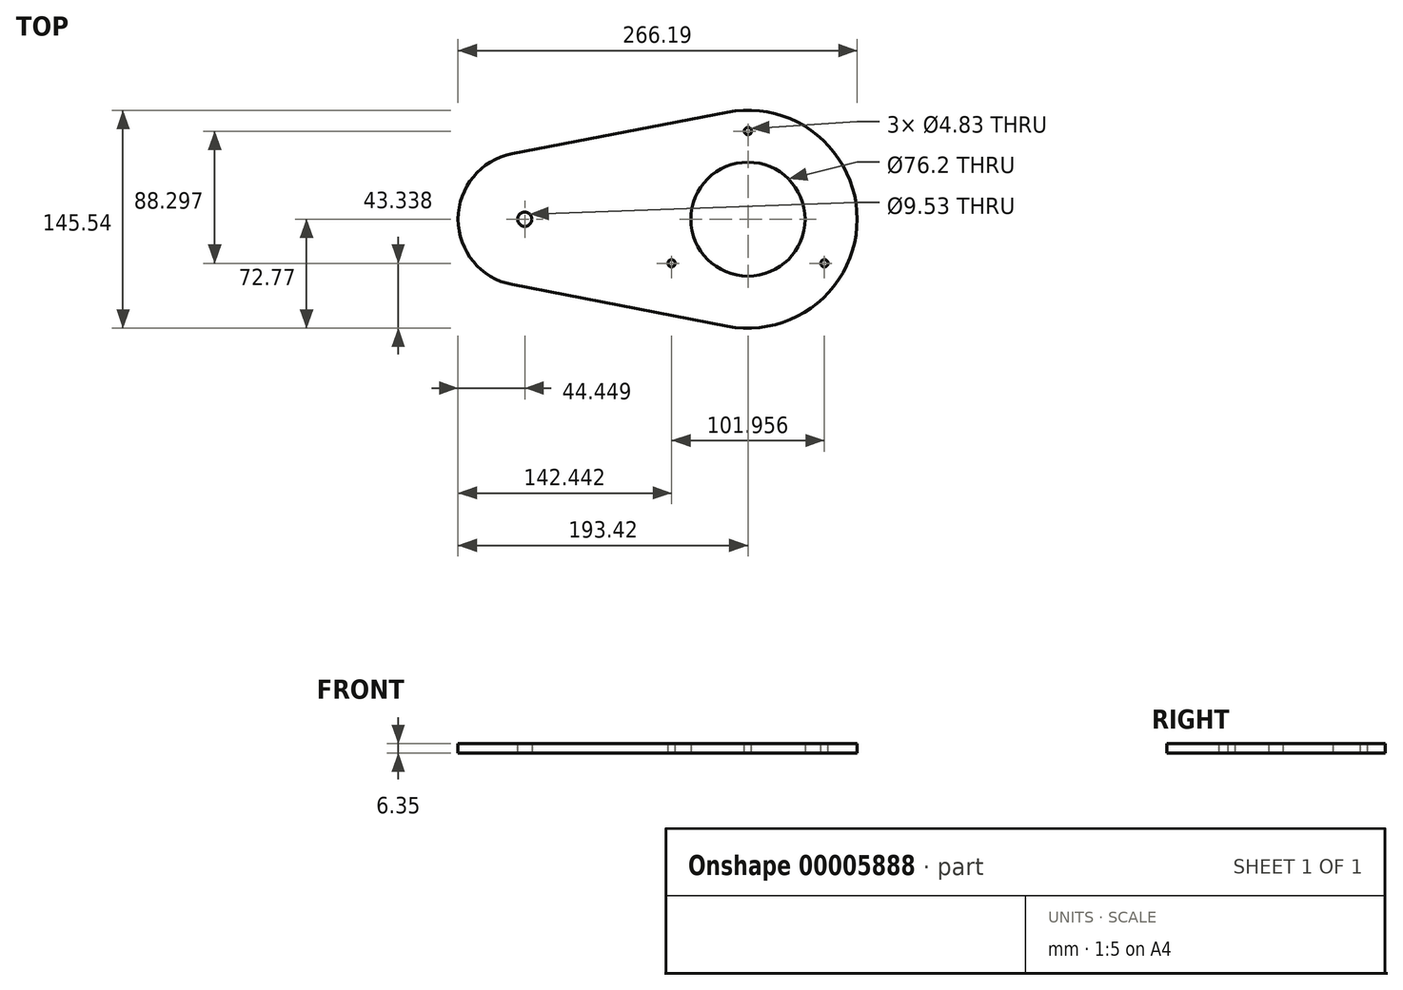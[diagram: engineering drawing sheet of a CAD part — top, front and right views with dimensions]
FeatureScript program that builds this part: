
annotation { "Feature Type Name" : "Feature", "Feature Type Description" : "" }
export const myFeature = defineFeature(function(context is Context, id is Id, definition is map)
    precondition{}
    {
        {
            var Q0;
            Q0=qCreatedBy(makeId("Top.planeOp"),FACE);
            var sketch = newSketch(context, id + "F0", { "sketchPlane" : qUnion([Q0])});
            skArc(sketch, "E0", {"start": v(-13.83, -71.44) * mm, "mid": v(72.77, 0) * mm, "end": v(-13.83, 71.44) * mm});
            skCircle(sketch, "E1", {"center": v(0, 0) * mm, "radius": 38.1 * mm});
            skLineSegment(sketch, "E2", {"start": v(0, 0) * mm, "end": v(-72.77, 0) * mm, "construction": true});
            skLineSegment(sketch, "E3", {"start": v(-72.77, 0) * mm, "end": v(-148.97, 0) * mm, "construction": true});
            skArc(sketch, "E4", {"start": v(-157.42, 43.64) * mm, "mid": v(-193.42, 0) * mm, "end": v(-157.42, -43.64) * mm});
            skLineSegment(sketch, "E5", {"start": v(-157.42, 43.64) * mm, "end": v(-13.83, 71.44) * mm});
            skLineSegment(sketch, "E6", {"start": v(-157.42, -43.64) * mm, "end": v(-13.83, -71.44) * mm});
            skCircle(sketch, "E7", {"center": v(-148.97, 0) * mm, "radius": 4.76 * mm});
            skSolve(sketch);
        }
        {
            var Q0;
            Q0=makeQuery(id+"F0.imprint","IMPRINT",FACE,{"disambiguationData":[TD([[makeQuery(id+"F0.imprint","IMPRINT",EDGE,{"derivedFrom":sQuery(id+"F0.wireOp",EDGE,"E0")}),1.0]])]});
            extrude(context, id + "F1", {"entities" : qUnion([Q0]), "depth" : 6.35 * mm});
        }
        {
            var Q0;
            Q0=makeQuery(id+"F1.opExtrude","CAP_FACE",FACE,{"disambiguationData":[OSD([sQuery(id+"F0.wireOp",EDGE,"E0"),sQuery(id+"F0.wireOp",EDGE,"E1"),sQuery(id+"F0.wireOp",EDGE,"7409aa68-249a-4d23-94e3-a1b410b62b42")])],"isStart":false});
            var sketch = newSketch(context, id + "F2", { "sketchPlane" : qUnion([Q0])});
            skLineSegment(sketch, "E8", {"start": v(0, 0) * mm, "end": v(0, 72.77) * mm, "construction": true});
            skCircle(sketch, "E9", {"center": v(0, 58.86) * mm, "radius": 4.76 * mm});
            skCircle(sketch, "E10.1.0", {"center": v(-50.98, -29.43) * mm, "radius": 4.76 * mm});
            skCircle(sketch, "E10.2.0", {"center": v(50.98, -29.43) * mm, "radius": 4.76 * mm});
            skPoint(sketch, "E10.center", {"position": v(0, 0) * mm});
            skCircle(sketch, "E11", {"center": v(0, 58.86) * mm, "radius": 2.41 * mm});
            skCircle(sketch, "E12.1.0", {"center": v(-50.98, -29.43) * mm, "radius": 2.41 * mm});
            skCircle(sketch, "E12.2.0", {"center": v(50.98, -29.43) * mm, "radius": 2.41 * mm});
            skSolve(sketch);
        }
        {
            var Q0;
            Q0=makeQuery(id+"F2.imprint","IMPRINT",FACE,{"disambiguationData":[TD([[makeQuery(id+"F2.imprint","IMPRINT",EDGE,{"derivedFrom":sQuery(id+"F2.wireOp",EDGE,"E12.1.0")}),1.0]])]});
            var Q1;
            Q1=makeQuery(id+"F2.imprint","IMPRINT",FACE,{"disambiguationData":[TD([[makeQuery(id+"F2.imprint","IMPRINT",EDGE,{"derivedFrom":sQuery(id+"F2.wireOp",EDGE,"E12.2.0")}),1.0]])]});
            var Q2;
            Q2=makeQuery(id+"F2.imprint","IMPRINT",FACE,{"disambiguationData":[TD([[makeQuery(id+"F2.imprint","IMPRINT",EDGE,{"derivedFrom":sQuery(id+"F2.wireOp",EDGE,"E11")}),1.0]])]});
            extrude(context, id + "F3", {"entities" : qUnion([Q0, Q1, Q2]), "operationType" : NewBodyOperationType.REMOVE, "endBound" : BoundingType.THROUGH_ALL, "oppositeDirection" : true, "depth" : 25.4 * mm});
        }
        {
            var Q0;
            Q0=makeQuery(id+"F1.opExtrude","CAP_FACE",FACE,{"disambiguationData":[OSD([sQuery(id+"F0.wireOp",EDGE,"E0"),sQuery(id+"F0.wireOp",EDGE,"E1"),sQuery(id+"F0.wireOp",EDGE,"7409aa68-249a-4d23-94e3-a1b410b62b42")])],"isStart":false});
            var sketch = newSketch(context, id + "F4", { "sketchPlane" : qUnion([Q0])});
            skCircle(sketch, "E13", {"center": v(0, 0) * mm, "radius": 17.78 * mm});
            skSolve(sketch);
        }
        {
            var Q0;
            Q0=makeQuery(id+"F1.opExtrude","CAP_FACE",FACE,{"disambiguationData":[OSD([sQuery(id+"F0.wireOp",EDGE,"E0"),sQuery(id+"F0.wireOp",EDGE,"E1"),sQuery(id+"F0.wireOp",EDGE,"7409aa68-249a-4d23-94e3-a1b410b62b42")])],"isStart":true});
            var sketch = newSketch(context, id + "F5", { "sketchPlane" : qUnion([Q0])});
            skCircle(sketch, "E14", {"center": v(0, 0) * mm, "radius": 18.41 * mm});
            skSolve(sketch);
        }
        {
            var Q0;
            Q0=makeQuery(id+"F5.imprint","IMPRINT",FACE,{"disambiguationData":[TD([[makeQuery(id+"F5.imprint","IMPRINT",EDGE,{"derivedFrom":sQuery(id+"F5.wireOp",EDGE,"E14")}),1.0]])]});
            extrude(context, id + "F6", {"entities" : qUnion([Q0]), "operationType" : NewBodyOperationType.REMOVE, "oppositeDirection" : true, "depth" : 1.59 * mm});
        }
    });
